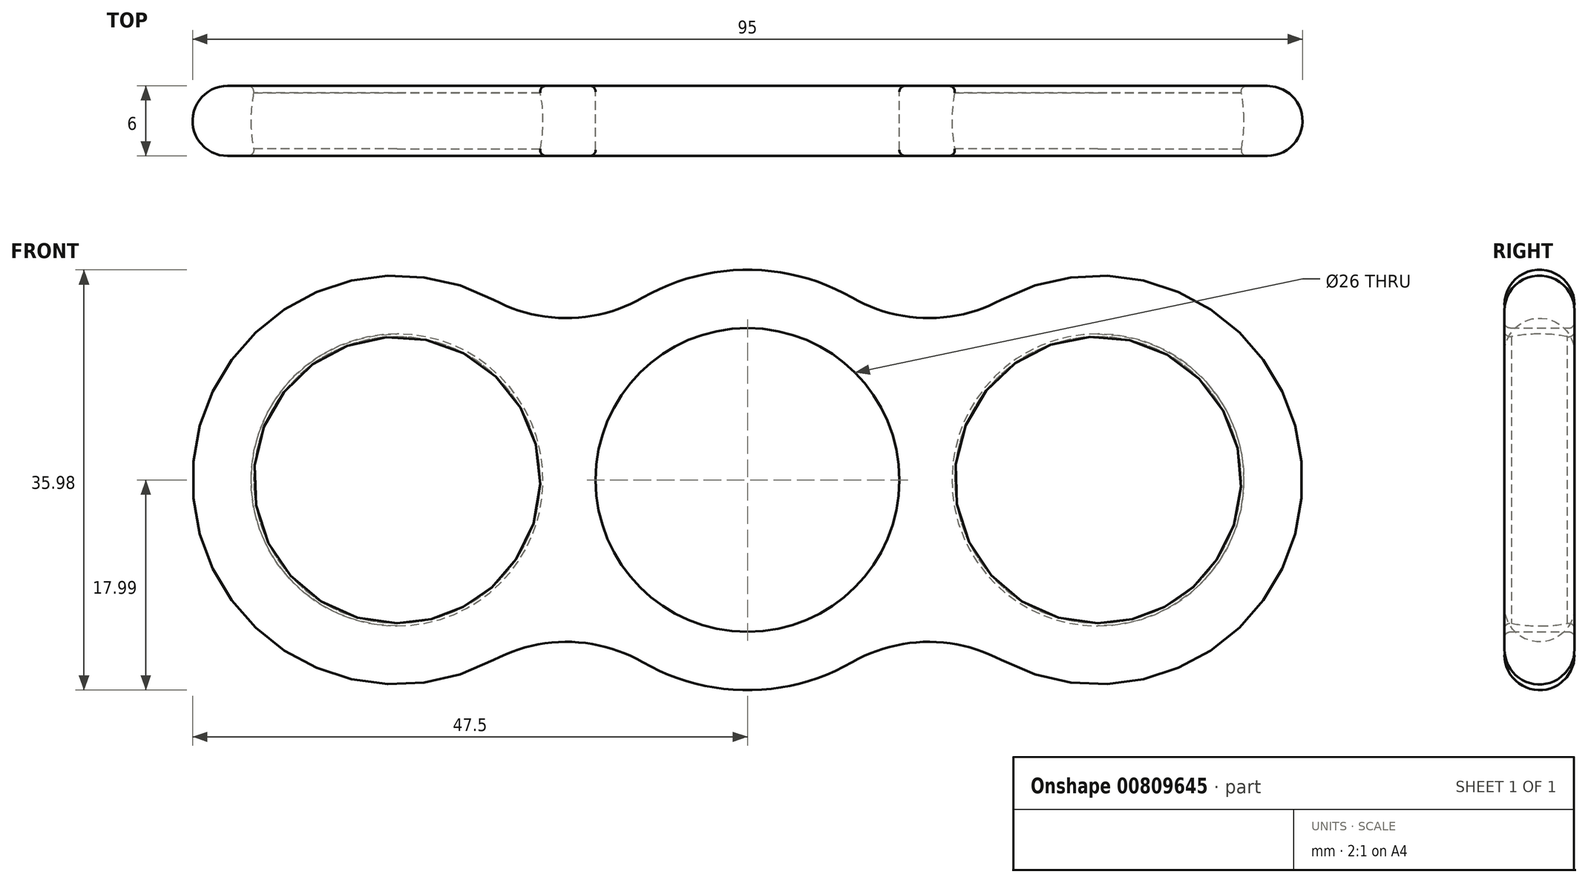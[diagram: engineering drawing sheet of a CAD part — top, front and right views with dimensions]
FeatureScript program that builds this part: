
annotation { "Feature Type Name" : "Feature", "Feature Type Description" : "" }
export const myFeature = defineFeature(function(context is Context, id is Id, definition is map)
    precondition{}
    {
        {
            var Q0;
            Q0=qCreatedBy(makeId("Front.planeOp"),FACE);
            var sketch = newSketch(context, id + "F0", { "sketchPlane" : qUnion([Q0])});
            skCircle(sketch, "E0", {"center": v(0, 0) * mm, "radius": 13 * mm});
            skLineSegment(sketch, "E1", {"start": v(0.9, 0) * mm, "end": v(30, 0) * mm, "construction": true});
            skArc(sketch, "E2.0", {"start": v(8.96, 15.6) * mm, "mid": v(0, 18) * mm, "end": v(-8.96, 15.6) * mm});
            skArc(sketch, "E3.trimOffspring", {"start": v(21.72, -15.42) * mm, "mid": v(47.5, 0) * mm, "end": v(21.72, 15.42) * mm});
            skArc(sketch, "E4", {"start": v(8.96, 15.6) * mm, "mid": v(15.32, 13.86) * mm, "end": v(21.72, 15.42) * mm});
            skArc(sketch, "E5.MirrorCS", {"start": v(8.96, -15.6) * mm, "mid": v(15.32, -13.86) * mm, "end": v(21.72, -15.42) * mm});
            skLineSegment(sketch, "E6", {"start": v(0, 0) * mm, "end": v(0, -26.47) * mm, "construction": true});
            skArc(sketch, "E7.MirrorCS", {"start": v(-8.96, -15.6) * mm, "mid": v(-15.32, -13.86) * mm, "end": v(-21.72, -15.42) * mm});
            skArc(sketch, "E8.MirrorCS", {"start": v(-21.72, -15.42) * mm, "mid": v(-47.5, 0) * mm, "end": v(-21.72, 15.42) * mm});
            skArc(sketch, "E9.MirrorCS", {"start": v(-8.96, 15.6) * mm, "mid": v(-15.32, 13.86) * mm, "end": v(-21.72, 15.42) * mm});
            skArc(sketch, "E10.trimOffspring", {"start": v(-8.96, -15.6) * mm, "mid": v(0, -18) * mm, "end": v(8.96, -15.6) * mm});
            skSolve(sketch);
        }
        {
            var Q0;
            Q0 = qSketchRegion(id + "F0", true);
            extrude(context, id + "F1", {"entities" : qUnion([Q0]), "depth" : 3 * mm, "offsetDistance" : 25 * mm, "hasSecondDirection" : true, "secondDirectionOppositeDirection" : true, "secondDirectionDepth" : 3 * mm});
        }
        {
            var Q0;
            Q0=qCreatedBy(makeId("Front.planeOp"),FACE);
            var sketch = newSketch(context, id + "F2", { "sketchPlane" : qUnion([Q0])});
            skLineSegment(sketch, "E11", {"start": v(0, 0) * mm, "end": v(-30, 0) * mm, "construction": true});
            skLineSegment(sketch, "E12", {"start": v(-30, 0) * mm, "end": v(-30, 30.5) * mm, "construction": true});
            skArc(sketch, "E13", {"start": v(-30, 12.5) * mm, "mid": v(-42.5, 0) * mm, "end": v(-30, -12.5) * mm});
            skLineSegment(sketch, "E14", {"start": v(-30, 12.5) * mm, "end": v(-30, -12.5) * mm});
            skSolve(sketch);
        }
        {
            var Q0;
            Q0 = qSketchRegion(id + "F2", true);
            var Q1;
            Q1=sQuery(id+"F2.wireOp",EDGE,"E12");
            revolve(context, id + "F3", {"operationType" : NewBodyOperationType.REMOVE, "surfaceOperationType" : NewSurfaceOperationType.NEW, "entities" : qUnion([Q0]), "axis" : qUnion([Q1]), "revolveType" : RevolveType.FULL, "oppositeDirection" : true});
        }
        {
            var Q0;
            Q0=qCreatedBy(makeId("Front.planeOp"),FACE);
            var sketch = newSketch(context, id + "F4", { "sketchPlane" : qUnion([Q0])});
            skLineSegment(sketch, "E15", {"start": v(0, 0) * mm, "end": v(30, 0) * mm, "construction": true});
            skArc(sketch, "E16", {"start": v(30, -12.5) * mm, "mid": v(42.5, 0) * mm, "end": v(30, 12.5) * mm});
            skLineSegment(sketch, "E17", {"start": v(30, 12.5) * mm, "end": v(30, -12.5) * mm});
            skLineSegment(sketch, "E18", {"start": v(30, 0) * mm, "end": v(30, 22.07) * mm, "construction": true});
            skSolve(sketch);
        }
        {
            var Q0;
            Q0 = qSketchRegion(id + "F4", true);
            var Q1;
            Q1=sQuery(id+"F4.wireOp",EDGE,"E18");
            revolve(context, id + "F5", {"operationType" : NewBodyOperationType.REMOVE, "surfaceOperationType" : NewSurfaceOperationType.NEW, "entities" : qUnion([Q0]), "axis" : qUnion([Q1]), "revolveType" : RevolveType.FULL});
        }
        {
            var Q0;
            Q0=makeQuery(id+"F3.boolean.opBoolean","INTERSECT",EDGE,{"derivedFrom":[makeQuery(id+"F1.opExtrude","CAP_FACE",FACE,{"disambiguationData":[OSD([sQuery(id+"F0.wireOp",EDGE,"E0"),sQuery(id+"F0.wireOp",EDGE,"E2.0"),sQuery(id+"F0.wireOp",EDGE,"E3.trimOffspring"),sQuery(id+"F0.wireOp",EDGE,"E4"),sQuery(id+"F0.wireOp",EDGE,"E5.MirrorCS"),sQuery(id+"F0.wireOp",EDGE,"E7.MirrorCS"),sQuery(id+"F0.wireOp",EDGE,"E8.MirrorCS"),sQuery(id+"F0.wireOp",EDGE,"E9.MirrorCS"),sQuery(id+"F0.wireOp",EDGE,"E10.trimOffspring")])],"isStart":false}),makeQuery(id+"F3.opRevolve","SWEPT_FACE",FACE,{"disambiguationData":[OSD([sQuery(id+"F2.wireOp",EDGE,"E13")])]})]});
            var Q1;
            Q1=makeQuery(id+"F3.boolean.opBoolean","INTERSECT",EDGE,{"derivedFrom":[makeQuery(id+"F1.opExtrude","CAP_FACE",FACE,{"disambiguationData":[OSD([sQuery(id+"F0.wireOp",EDGE,"E0"),sQuery(id+"F0.wireOp",EDGE,"E2.0"),sQuery(id+"F0.wireOp",EDGE,"E3.trimOffspring"),sQuery(id+"F0.wireOp",EDGE,"E4"),sQuery(id+"F0.wireOp",EDGE,"E5.MirrorCS"),sQuery(id+"F0.wireOp",EDGE,"E7.MirrorCS"),sQuery(id+"F0.wireOp",EDGE,"E8.MirrorCS"),sQuery(id+"F0.wireOp",EDGE,"E9.MirrorCS"),sQuery(id+"F0.wireOp",EDGE,"E10.trimOffspring")])],"isStart":true}),makeQuery(id+"F3.opRevolve","SWEPT_FACE",FACE,{"disambiguationData":[OSD([sQuery(id+"F2.wireOp",EDGE,"E13")])]})]});
            var Q2;
            Q2=makeQuery(id+"F1.opExtrude","CAP_EDGE",EDGE,{"disambiguationData":[OSD([sQuery(id+"F0.wireOp",EDGE,"E0")])],"isStart":true});
            var Q3;
            Q3=makeQuery(id+"F1.opExtrude","CAP_EDGE",EDGE,{"disambiguationData":[OSD([sQuery(id+"F0.wireOp",EDGE,"E0")])],"isStart":false});
            var Q4;
            Q4=makeQuery(id+"F5.boolean.opBoolean","INTERSECT",EDGE,{"derivedFrom":[makeQuery(id+"F1.opExtrude","CAP_FACE",FACE,{"disambiguationData":[OSD([sQuery(id+"F0.wireOp",EDGE,"E0"),sQuery(id+"F0.wireOp",EDGE,"E2.0"),sQuery(id+"F0.wireOp",EDGE,"E3.trimOffspring"),sQuery(id+"F0.wireOp",EDGE,"E4"),sQuery(id+"F0.wireOp",EDGE,"E5.MirrorCS"),sQuery(id+"F0.wireOp",EDGE,"E7.MirrorCS"),sQuery(id+"F0.wireOp",EDGE,"E8.MirrorCS"),sQuery(id+"F0.wireOp",EDGE,"E9.MirrorCS"),sQuery(id+"F0.wireOp",EDGE,"E10.trimOffspring")])],"isStart":false}),makeQuery(id+"F5.opRevolve","SWEPT_FACE",FACE,{"disambiguationData":[OSD([sQuery(id+"F4.wireOp",EDGE,"E16")])]})]});
            var Q5;
            Q5=makeQuery(id+"F5.boolean.opBoolean","INTERSECT",EDGE,{"derivedFrom":[makeQuery(id+"F1.opExtrude","CAP_FACE",FACE,{"disambiguationData":[OSD([sQuery(id+"F0.wireOp",EDGE,"E0"),sQuery(id+"F0.wireOp",EDGE,"E2.0"),sQuery(id+"F0.wireOp",EDGE,"E3.trimOffspring"),sQuery(id+"F0.wireOp",EDGE,"E4"),sQuery(id+"F0.wireOp",EDGE,"E5.MirrorCS"),sQuery(id+"F0.wireOp",EDGE,"E7.MirrorCS"),sQuery(id+"F0.wireOp",EDGE,"E8.MirrorCS"),sQuery(id+"F0.wireOp",EDGE,"E9.MirrorCS"),sQuery(id+"F0.wireOp",EDGE,"E10.trimOffspring")])],"isStart":true}),makeQuery(id+"F5.opRevolve","SWEPT_FACE",FACE,{"disambiguationData":[OSD([sQuery(id+"F4.wireOp",EDGE,"E16")])]})]});
            fillet(context, id + "F6", {"entities" : qUnion([Q0, Q1, Q2, Q3, Q4, Q5]), "radius" : .5 * mm, "tangentPropagation" : true, "allowEdgeOverflow" : false});
        }
        {
            var Q0;
            Q0=makeQuery(id+"F1.opExtrude","CAP_EDGE",EDGE,{"disambiguationData":[OSD([sQuery(id+"F0.wireOp",EDGE,"E3.trimOffspring")])],"isStart":true});
            var Q1;
            Q1=makeQuery(id+"F1.opExtrude","CAP_EDGE",EDGE,{"disambiguationData":[OSD([sQuery(id+"F0.wireOp",EDGE,"E3.trimOffspring")])],"isStart":false});
            fillet(context, id + "F7", {"entities" : qUnion([Q0, Q1]), "radius" : 3 * mm, "tangentPropagation" : true, "allowEdgeOverflow" : false});
        }
    });
